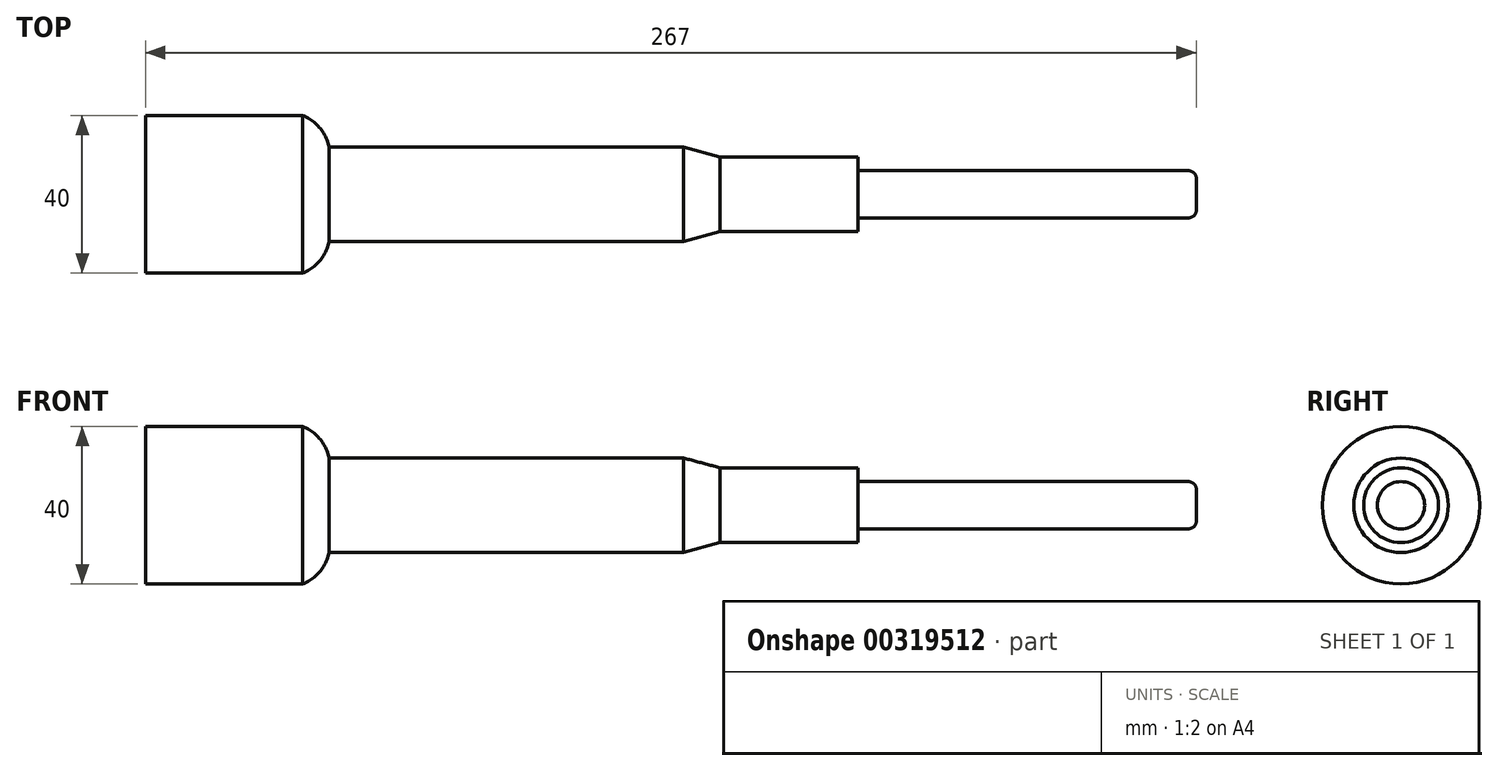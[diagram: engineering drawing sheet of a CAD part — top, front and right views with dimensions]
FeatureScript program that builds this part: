
annotation { "Feature Type Name" : "Feature", "Feature Type Description" : "" }
export const myFeature = defineFeature(function(context is Context, id is Id, definition is map)
    precondition{}
    {
        {
            var Q0;
            Q0=qCreatedBy(makeId("Front.planeOp"),FACE);
            var sketch = newSketch(context, id + "F0", { "sketchPlane" : qUnion([Q0])});
            skLineSegment(sketch, "E0", {"start": v(0, 0) * mm, "end": v(267, 0) * mm, "construction": true});
            skLineSegment(sketch, "E1", {"start": v(267, 0) * mm, "end": v(267, 6) * mm});
            skLineSegment(sketch, "E2", {"start": v(267, 6) * mm, "end": v(181, 6) * mm});
            skLineSegment(sketch, "E3", {"start": v(181, 6) * mm, "end": v(181, 9.5) * mm});
            skLineSegment(sketch, "E4", {"start": v(181, 9.5) * mm, "end": v(146, 9.5) * mm});
            skLineSegment(sketch, "E5", {"start": v(0, 0) * mm, "end": v(0, 20) * mm});
            skLineSegment(sketch, "E6", {"start": v(0, 20) * mm, "end": v(40, 20) * mm});
            skLineSegment(sketch, "E7", {"start": v(146, 9.5) * mm, "end": v(136.67, 12) * mm});
            skLineSegment(sketch, "E8", {"start": v(136.67, 12) * mm, "end": v(46.67, 12) * mm});
            skArc(sketch, "E9", {"start": v(46.67, 12) * mm, "mid": v(44.34, 16.84) * mm, "end": v(40, 20) * mm});
            skLineSegment(sketch, "E10", {"start": v(0, 0) * mm, "end": v(267, 0) * mm});
            skSolve(sketch);
        }
        {
            var Q0;
            Q0=makeQuery(id+"F0.imprint","IMPRINT",FACE,{"disambiguationData":[TD([[makeQuery(id+"F0.imprint","IMPRINT",EDGE,{"derivedFrom":sQuery(id+"F0.wireOp",EDGE,"E1")}),1.0]])]});
            var Q1;
            Q1=sQuery(id+"F0.wireOp",EDGE,"E10");
            revolve(context, id + "F1", {"entities" : qUnion([Q0]), "axis" : qUnion([Q1]), "revolveType" : RevolveType.FULL});
        }
        {
            var Q0;
            Q0=makeQuery(id+"F1.opRevolve","SWEPT_EDGE",EDGE,{"disambiguationData":[OSD([sQuery(id+"F0.wireOp",EDGE,"E1"),sQuery(id+"F0.wireOp",EDGE,"E2")])]});
            fillet(context, id + "F2", {"entities" : qUnion([Q0]), "radius" : 2 * mm, "tangentPropagation" : true, "allowEdgeOverflow" : false});
        }
    });
